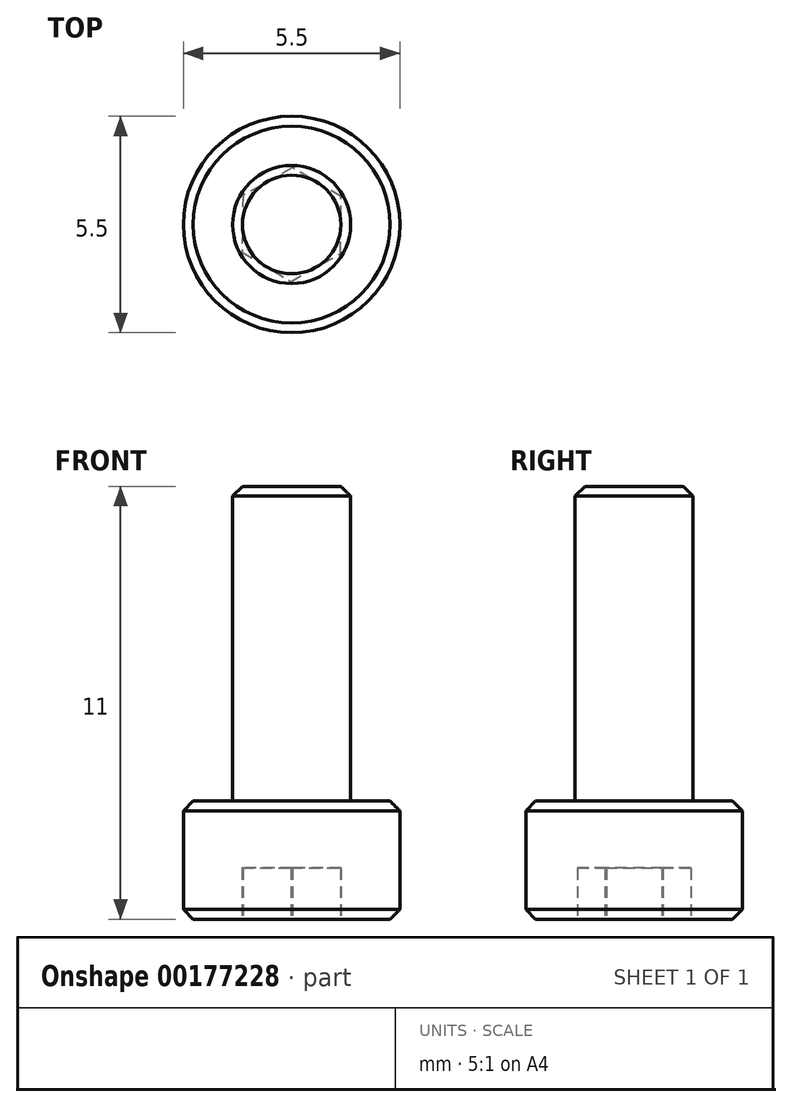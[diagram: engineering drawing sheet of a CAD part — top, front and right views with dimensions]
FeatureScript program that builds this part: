
annotation { "Feature Type Name" : "Feature", "Feature Type Description" : "" }
export const myFeature = defineFeature(function(context is Context, id is Id, definition is map)
    precondition{}
    {
        {
            var Q0;
            Q0=qCreatedBy(makeId("Top.planeOp"),FACE);
            var sketch = newSketch(context, id + "F0", { "sketchPlane" : qUnion([Q0])});
            skCircle(sketch, "E0", {"center": v(0, 0) * mm, "radius": 1.5 * mm});
            skSolve(sketch);
        }
        {
            var Q0;
            Q0 = qSketchRegion(id + "F0", true);
            extrude(context, id + "F1", {"entities" : qUnion([Q0]), "depth" : 8 * mm});
        }
        {
            var Q0;
            Q0=qCreatedBy(makeId("Top.planeOp"),FACE);
            var sketch = newSketch(context, id + "F2", { "sketchPlane" : qUnion([Q0])});
            skCircle(sketch, "E1", {"center": v(0, 0) * mm, "radius": 2.75 * mm});
            skSolve(sketch);
        }
        {
            var Q0;
            Q0 = qSketchRegion(id + "F2", true);
            extrude(context, id + "F3", {"entities" : qUnion([Q0]), "operationType" : NewBodyOperationType.ADD, "oppositeDirection" : true, "depth" : 3 * mm});
        }
        {
            var Q0;
            Q0=makeQuery(id+"F3.opExtrude","CAP_FACE",FACE,{"disambiguationData":[OSD([sQuery(id+"F2.wireOp",EDGE,"E1")])],"isStart":false});
            var sketch = newSketch(context, id + "F4", { "sketchPlane" : qUnion([Q0])});
            skCircle(sketch, "E2.cCircle", {"center": v(0, 0) * mm, "radius": 1.25 * mm, "construction": true});
            skLineSegment(sketch, "E2.0", {"start": v(1.26, -0.7) * mm, "end": v(0.02, -1.44) * mm});
            skLineSegment(sketch, "E2.1", {"start": v(0.02, -1.44) * mm, "end": v(-1.24, -0.74) * mm});
            skLineSegment(sketch, "E2.2", {"start": v(-1.24, -0.74) * mm, "end": v(-1.26, 0.7) * mm});
            skLineSegment(sketch, "E2.3", {"start": v(-1.26, 0.7) * mm, "end": v(-0.02, 1.44) * mm});
            skLineSegment(sketch, "E2.4", {"start": v(-0.02, 1.44) * mm, "end": v(1.24, 0.74) * mm});
            skLineSegment(sketch, "E2.5", {"start": v(1.24, 0.74) * mm, "end": v(1.26, -0.7) * mm});
            skPoint(sketch, "E2.0.midPoint", {"position": v(0.64, -1.07) * mm});
            skSolve(sketch);
        }
        {
            var Q0;
            Q0 = qSketchRegion(id + "F4", true);
            extrude(context, id + "F5", {"entities" : qUnion([Q0]), "operationType" : NewBodyOperationType.REMOVE, "oppositeDirection" : true, "depth" : 1.3 * mm});
        }
        {
            var Q0;
            Q0=makeQuery(id+"F3.opExtrude","CAP_EDGE",EDGE,{"disambiguationData":[OSD([sQuery(id+"F2.wireOp",EDGE,"E1")])],"isStart":false});
            var Q1;
            Q1=makeQuery(id+"F3.opExtrude","CAP_EDGE",EDGE,{"disambiguationData":[OSD([sQuery(id+"F2.wireOp",EDGE,"E1")])],"isStart":true});
            var Q2;
            Q2=makeQuery(id+"F1.opExtrude","CAP_EDGE",EDGE,{"disambiguationData":[OSD([sQuery(id+"F0.wireOp",EDGE,"E0")])],"isStart":false});
            chamfer(context, id + "F6", {"entities" : qUnion([Q0, Q1, Q2]), "width" : .25 * mm, "tangentPropagation" : true});
        }
    });
